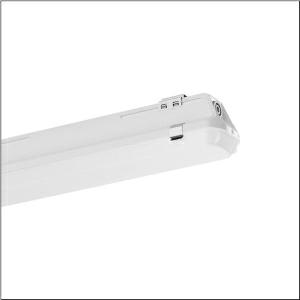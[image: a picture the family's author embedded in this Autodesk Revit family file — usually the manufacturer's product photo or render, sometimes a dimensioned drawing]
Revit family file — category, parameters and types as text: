
# Revit family: monsun_r__21_51fb20mp480b_5a94
name_source: partatom
category: Lighting Fixtures
units: mm (PartAtom-declared; Revit-internal decimal feet)

## family parameters
Cut with Voids When Loaded = No
Host = Face
Light Source = No
Part Type = Normal
Room Calculation Point = No
Round Connector Dimension = Use Diameter
Shared = No

## types (1)
- --- (1 x LED, 7370 lm, 53.6 W, 4000K)
    Apparent Load = 54 VA
    CIE Flux Codes = 45 75 93 94 100
    Color Rendering = 80
    Color Temperature = 4000K
    Default Elevation = 1800 mm
    Description = Monsun® 21, damp-proof luminaire, chain hanger, primary optical cover: enclosure, of PC, light emission: direct distribution, primary light characteristic: symmetric, installation type: suspended mounting, surface-mounted, horizontal mounting, vertical mounting, LED, rated luminous flux: 7.370lm, luminous efficacy: 138lm/W, light colour: 840, colour temperature: 4000K, control gear: ECG, with terminal, 3-pole, max. 2.5mm², mains connection: 220..240V, AC, 50/60Hz, rated input power: 54W, housing, of glass-fibre reinforced polyester, uncoated, bright grey, incl. chain hanger, length: 1.590mm, width: 90mm, height: 88mm, clip for enclosure, of stainless steel (V2A), ceiling mounting element, of stainless steel (V2A), chain hanger, of stainless steel (V2A), protection rating (complete): IP66, insulation class (complete): insulation class I (protective earthing), certification: CE, ENEC, VDE, UKCA, protection symbol: D, impact resistance: IK08, permissible operating ambient temperature: -25..+35°C, standard: EN 50419, EN 60598-2-1, corresponds to IFS (International Featured Standards) requirements for safety and quality in the food industry, for indoor or canopied outdoor use, no direct snow, no direct sun, no direct rain, contact your sales advisor before using the luminaires in applications with unclear chemical exposure, large temperature fluctuations or condensation-forming humidity, LABS conformity tested according to VDMA 24364:2018-05, packaging unit: 1 piece
    Height = 89 mm
    Lamp = 1 x LED
    Lamp Light Flux = 7370 lm
    Lamp Power = 53.6 W
    Lamp count = 1
    Length = 1590 mm
    Luminous efficacy = 138 lm/W
    Manufacturer = Siteco
    ModVariant = No
    Model = 51FB20MP480B
    Mounting Place = Ceiling
    Mounting Type = Surface mounted
    Number of Poles = 1
    OnlyDefault = Yes
    Power Factor = 1
    Product Name = Monsun® 21
    Product group = damp-proof luminaire
    ProductGroupID = 301
    Protection Class = Protection class I
    Protection Degree = IP 66
    RLX_Detail_Level = 1
    RLX_Emergency_Light_Flux = 0 lm
    RLX_Emergency_Type = 0
    RLX_Emergency_Type_DB = No
    RlxData = <blob elided: 89613 chars, md5=f512cdf4>
    Socket = socket
    Standby Power = 0 W
    System Light Flux = 7370 lm
    System Power = 54 W
    Type Comments = factory setting: luminous flux: 100 % | (A | C | E) | 121 mA
    Type Image = l_1006717.jpg
    URL = http://relux.com
    VarID = @adj_096919
    Voltage = 0 V
    Weight = 0.00 kg
    Width = 90 mm

## geometry (parser evidence)
native form markers: Blend x4, Sweep x14
no freeform markers — native parametric forms only
